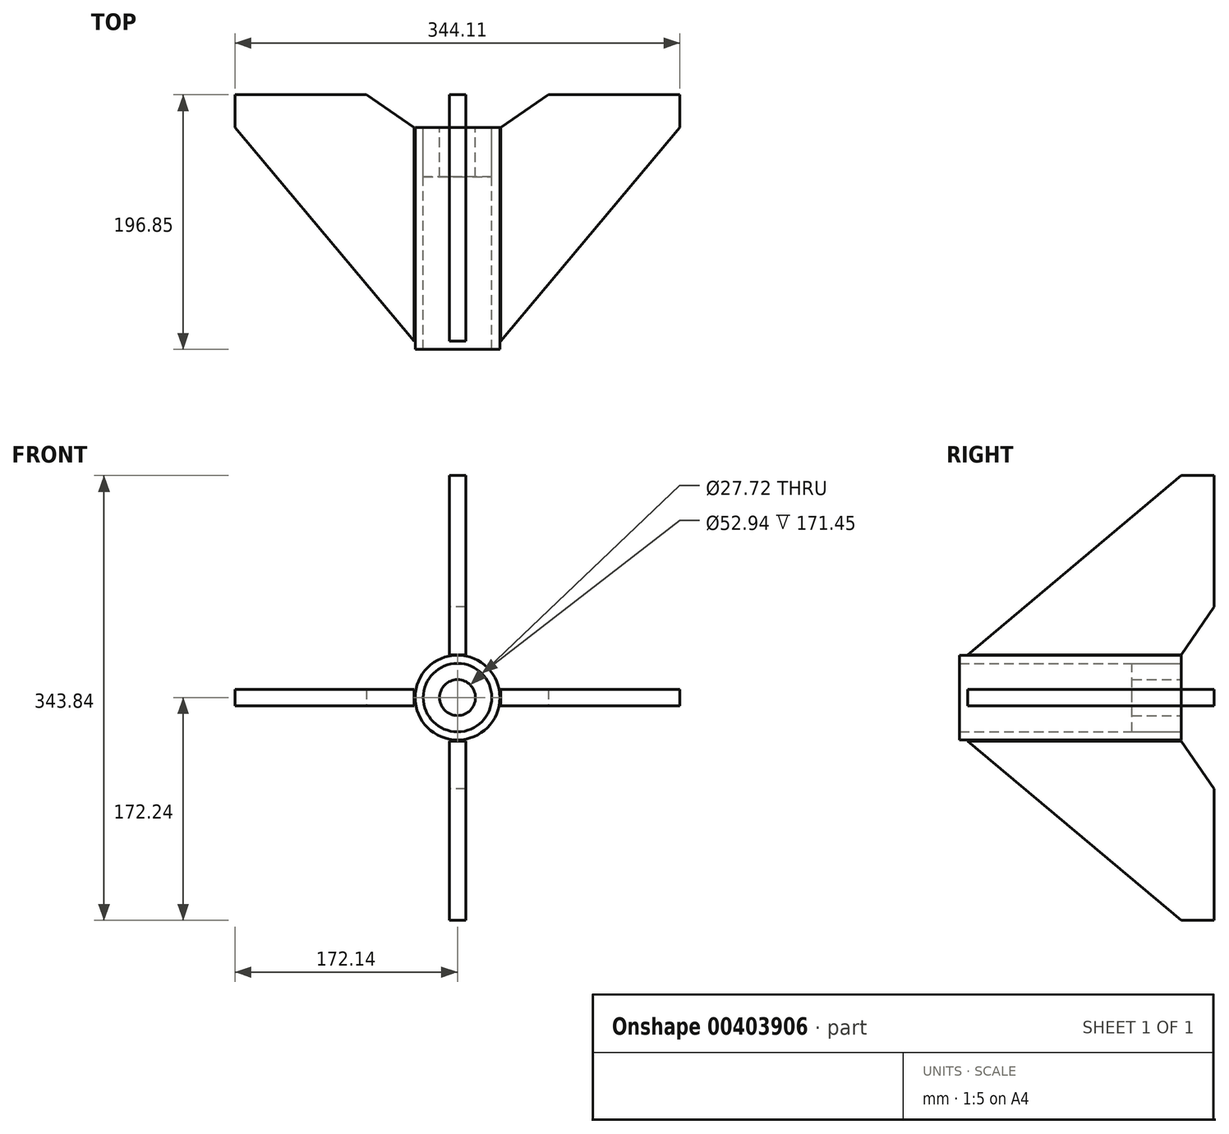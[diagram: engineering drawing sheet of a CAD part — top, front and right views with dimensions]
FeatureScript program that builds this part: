
annotation { "Feature Type Name" : "Feature", "Feature Type Description" : "" }
export const myFeature = defineFeature(function(context is Context, id is Id, definition is map)
    precondition{}
    {
        {
            var Q0;
            Q0=qCreatedBy(makeId("Front.planeOp"),FACE);
            var sketch = newSketch(context, id + "F0", { "sketchPlane" : qUnion([Q0])});
            skCircle(sketch, "E0", {"center": v(0, 0) * mm, "radius": 32.78 * mm});
            skCircle(sketch, "E1", {"center": v(0, 0) * mm, "radius": 26.47 * mm});
            skLineSegment(sketch, "E2", {"start": v(0, -76.2) * mm, "end": v(0, 76.2) * mm});
            skCircle(sketch, "E3", {"center": v(0, 0) * mm, "radius": 13.86 * mm});
            skSolve(sketch);
        }
        {
            var Q0;
            {var subQ0=sQuery(id+"F0.wireOp",EDGE,"E2");var subQ1=sQuery(id+"F0.wireOp",EDGE,"E0");var subQ2=makeQuery(id+"F0.imprint","INTERSECT",VERTEX,{"disambiguationData":[OD(1.0)],"derivedFrom":[subQ1,subQ0]});Q0=makeQuery(id+"F0.imprint","IMPRINT",FACE,{"disambiguationData":[TD([[makeQuery(id+"F0.imprint","IMPRINT",EDGE,{"disambiguationData":[TD([[subQ2,-1.0]])],"derivedFrom":subQ1}),1.0]])]});}
            var Q1;
            {var subQ0=sQuery(id+"F0.wireOp",EDGE,"E2");var subQ1=sQuery(id+"F0.wireOp",EDGE,"E0");var subQ2=makeQuery(id+"F0.imprint","INTERSECT",VERTEX,{"disambiguationData":[OD(1.0)],"derivedFrom":[subQ1,subQ0]});Q1=makeQuery(id+"F0.imprint","IMPRINT",FACE,{"disambiguationData":[TD([[makeQuery(id+"F0.imprint","IMPRINT",EDGE,{"disambiguationData":[TD([[subQ2,1.0]])],"derivedFrom":subQ1}),1.0]])]});}
            var Q2;
            {var subQ0=sQuery(id+"F0.wireOp",EDGE,"5oPWdtzy-OPul-B56H-vmQn-ATjjeZZYbcvi");var subQ1=sQuery(id+"F0.wireOp",EDGE,"E0");var subQ2=makeQuery(id+"F0.imprint","INTERSECT",VERTEX,{"disambiguationData":[OD(1.0)],"derivedFrom":[subQ1,subQ0]});Q2=makeQuery(id+"F0.imprint","IMPRINT",FACE,{"disambiguationData":[TD([[makeQuery(id+"F0.imprint","IMPRINT",EDGE,{"disambiguationData":[TD([[subQ2,-1.0]])],"derivedFrom":subQ1}),1.0]])]});}
            var Q3;
            {var subQ0=sQuery(id+"F0.wireOp",EDGE,"5oPWdtzy-OPul-B56H-vmQn-ATjjeZZYbcvi");var subQ1=sQuery(id+"F0.wireOp",EDGE,"E0");var subQ2=makeQuery(id+"F0.imprint","INTERSECT",VERTEX,{"disambiguationData":[OD(0.0)],"derivedFrom":[subQ1,subQ0]});Q3=makeQuery(id+"F0.imprint","IMPRINT",FACE,{"disambiguationData":[TD([[makeQuery(id+"F0.imprint","IMPRINT",EDGE,{"disambiguationData":[TD([[subQ2,1.0]])],"derivedFrom":subQ1}),1.0]])]});}
            var Q4;
            {var subQ0=sQuery(id+"F0.wireOp",EDGE,"E2");var subQ1=sQuery(id+"F0.wireOp",EDGE,"E0");var subQ2=makeQuery(id+"F0.imprint","INTERSECT",VERTEX,{"disambiguationData":[OD(0.0)],"derivedFrom":[subQ1,subQ0]});Q4=makeQuery(id+"F0.imprint","IMPRINT",FACE,{"disambiguationData":[TD([[makeQuery(id+"F0.imprint","IMPRINT",EDGE,{"disambiguationData":[TD([[subQ2,1.0]])],"derivedFrom":subQ1}),1.0]])]});}
            var Q5;
            {var subQ0=sQuery(id+"F0.wireOp",EDGE,"1dQYtLTc-Qprp-vLL3-yUOJ-yKbSne6VpX0o");var subQ1=sQuery(id+"F0.wireOp",EDGE,"E0");var subQ2=makeQuery(id+"F0.imprint","INTERSECT",VERTEX,{"disambiguationData":[OD(0.0)],"derivedFrom":[subQ1,subQ0]});Q5=makeQuery(id+"F0.imprint","IMPRINT",FACE,{"disambiguationData":[TD([[makeQuery(id+"F0.imprint","IMPRINT",EDGE,{"disambiguationData":[TD([[subQ2,1.0]])],"derivedFrom":subQ1}),1.0]])]});}
            var Q6;
            {var subQ0=sQuery(id+"F0.wireOp",EDGE,"E2");var subQ1=sQuery(id+"F0.wireOp",EDGE,"E0");var subQ2=makeQuery(id+"F0.imprint","INTERSECT",VERTEX,{"disambiguationData":[OD(0.0)],"derivedFrom":[subQ1,subQ0]});Q6=makeQuery(id+"F0.imprint","IMPRINT",FACE,{"disambiguationData":[TD([[makeQuery(id+"F0.imprint","IMPRINT",EDGE,{"disambiguationData":[TD([[subQ2,-1.0]])],"derivedFrom":subQ1}),1.0]])]});}
            var Q7;
            {var subQ0=sQuery(id+"F0.wireOp",EDGE,"1dQYtLTc-Qprp-vLL3-yUOJ-yKbSne6VpX0o");var subQ1=sQuery(id+"F0.wireOp",EDGE,"E0");var subQ2=makeQuery(id+"F0.imprint","INTERSECT",VERTEX,{"disambiguationData":[OD(1.0)],"derivedFrom":[subQ1,subQ0]});Q7=makeQuery(id+"F0.imprint","IMPRINT",FACE,{"disambiguationData":[TD([[makeQuery(id+"F0.imprint","IMPRINT",EDGE,{"disambiguationData":[TD([[subQ2,-1.0]])],"derivedFrom":subQ1}),1.0]])]});}
            extrude(context, id + "F1", {"entities" : qUnion([Q0, Q1, Q2, Q3, Q4, Q5, Q6, Q7]), "depth" : 171.45 * mm});
        }
        {
            var Q0;
            Q0=qCreatedBy(makeId("Right.planeOp"),FACE);
            var sketch = newSketch(context, id + "F2", { "sketchPlane" : qUnion([Q0])});
            skLineSegment(sketch, "E4", {"start": v(-165.1, -33.7) * mm, "end": v(0, -172.24) * mm});
            skLineSegment(sketch, "E5", {"start": v(-165.1, -33.7) * mm, "end": v(0, -33.7) * mm});
            skPoint(sketch, "E6", {"position": v(-165.1, 33.07) * mm});
            skLineSegment(sketch, "E7", {"start": v(-165.1, 33.07) * mm, "end": v(0, 171.6) * mm});
            skLineSegment(sketch, "E8", {"start": v(0, 33.07) * mm, "end": v(25.4, 70) * mm});
            skLineSegment(sketch, "E9", {"start": v(0, 171.6) * mm, "end": v(0, 33.07) * mm});
            skLineSegment(sketch, "E10", {"start": v(25.4, 70) * mm, "end": v(25.4, 171.6) * mm});
            skLineSegment(sketch, "E11", {"start": v(25.4, 171.6) * mm, "end": v(0, 171.6) * mm});
            skLineSegment(sketch, "E12", {"start": v(-165.1, 33.07) * mm, "end": v(0, 33.07) * mm});
            skLineSegment(sketch, "E13", {"start": v(0, -172.24) * mm, "end": v(25.4, -172.24) * mm});
            skLineSegment(sketch, "E14", {"start": v(25.4, -172.24) * mm, "end": v(25.4, -70.64) * mm});
            skLineSegment(sketch, "E15", {"start": v(25.4, -70.64) * mm, "end": v(0, -33.7) * mm});
            skSolve(sketch);
        }
        {
            var Q0;
            Q0=makeQuery(id+"F2.imprint","IMPRINT",FACE,{"disambiguationData":[TD([[makeQuery(id+"F2.imprint","IMPRINT",EDGE,{"derivedFrom":sQuery(id+"F2.wireOp",EDGE,"E4")}),1.0]])]});
            var Q1;
            Q1=makeQuery(id+"F2.imprint","IMPRINT",FACE,{"disambiguationData":[TD([[makeQuery(id+"F2.imprint","IMPRINT",EDGE,{"derivedFrom":sQuery(id+"F2.wireOp",EDGE,"8KpwZqoE-Ewsf-Pob2-hUoS-TpSoyfrnr4qn")}),1.0]])]});
            var Q2;
            Q2=makeQuery(id+"F2.imprint","IMPRINT",FACE,{"disambiguationData":[TD([[makeQuery(id+"F2.imprint","IMPRINT",EDGE,{"derivedFrom":sQuery(id+"F2.wireOp",EDGE,"E7")}),-1.0]])]});
            var Q3;
            Q3=makeQuery(id+"F2.imprint","IMPRINT",FACE,{"disambiguationData":[TD([[makeQuery(id+"F2.imprint","IMPRINT",EDGE,{"derivedFrom":sQuery(id+"F2.wireOp",EDGE,"E8")}),1.0]])]});
            extrude(context, id + "F3", {"entities" : qUnion([Q0, Q1, Q2, Q3]), "endBound" : BoundingType.SYMMETRIC, "depth" : 12.7 * mm});
        }
        {
            var Q0;
            Q0=qCreatedBy(makeId("Top.planeOp"),FACE);
            var sketch = newSketch(context, id + "F4", { "sketchPlane" : qUnion([Q0])});
            skPoint(sketch, "E16", {"position": v(33.43, -165.1) * mm});
            skPoint(sketch, "E17", {"position": v(33.43, 0) * mm});
            skLineSegment(sketch, "E18", {"start": v(33.43, -165.1) * mm, "end": v(33.43, 0) * mm});
            skLineSegment(sketch, "E19", {"start": v(33.43, -165.1) * mm, "end": v(171.97, 0) * mm});
            skLineSegment(sketch, "E20", {"start": v(33.43, 0) * mm, "end": v(70.37, 25.4) * mm});
            skLineSegment(sketch, "E21", {"start": v(171.97, 0) * mm, "end": v(171.97, 25.4) * mm});
            skLineSegment(sketch, "E22", {"start": v(171.97, 25.4) * mm, "end": v(70.37, 25.4) * mm});
            skLineSegment(sketch, "E23", {"start": v(-33.6, -165.1) * mm, "end": v(-172.14, 0) * mm});
            skLineSegment(sketch, "E24", {"start": v(-172.14, 0) * mm, "end": v(-172.14, 25.4) * mm});
            skLineSegment(sketch, "E25", {"start": v(-172.14, 25.4) * mm, "end": v(-70.54, 25.4) * mm});
            skLineSegment(sketch, "E26", {"start": v(-70.54, 25.4) * mm, "end": v(-33.6, 0) * mm});
            skLineSegment(sketch, "E27", {"start": v(-33.6, 0) * mm, "end": v(-172.14, 0) * mm});
            skLineSegment(sketch, "E28", {"start": v(-33.6, 0) * mm, "end": v(-33.6, -165.1) * mm});
            skLineSegment(sketch, "E29", {"start": v(171.97, 0) * mm, "end": v(33.43, 0) * mm});
            skSolve(sketch);
        }
        {
            var Q0;
            {var subQ0=sQuery(id+"F4.wireOp",EDGE,"E20");Q0=makeQuery(id+"F4.imprint","IMPRINT",FACE,{"disambiguationData":[TD([[makeQuery(id+"F4.imprint","IMPRINT",EDGE,{"derivedFrom":subQ0}),-1.0]])]});}
            var Q1;
            {var subQ0=sQuery(id+"F4.wireOp",EDGE,"E18");Q1=makeQuery(id+"F4.imprint","IMPRINT",FACE,{"disambiguationData":[TD([[makeQuery(id+"F4.imprint","IMPRINT",EDGE,{"derivedFrom":subQ0}),-1.0]])]});}
            var Q2;
            Q2=makeQuery(id+"F4.imprint","IMPRINT",FACE,{"disambiguationData":[TD([[makeQuery(id+"F4.imprint","IMPRINT",EDGE,{"derivedFrom":sQuery(id+"F4.wireOp",EDGE,"E24")}),-1.0]])]});
            var Q3;
            Q3=makeQuery(id+"F4.imprint","IMPRINT",FACE,{"disambiguationData":[TD([[makeQuery(id+"F4.imprint","IMPRINT",EDGE,{"derivedFrom":sQuery(id+"F4.wireOp",EDGE,"E23")}),-1.0]])]});
            extrude(context, id + "F5", {"entities" : qUnion([Q0, Q1, Q2, Q3]), "operationType" : NewBodyOperationType.ADD, "endBound" : BoundingType.SYMMETRIC, "depth" : 12.7 * mm});
        }
        {
            var Q0;
            {var subQ0=sQuery(id+"F0.wireOp",EDGE,"E2");var subQ1=sQuery(id+"F0.wireOp",EDGE,"E1");var subQ2=makeQuery(id+"F0.imprint","INTERSECT",VERTEX,{"disambiguationData":[OD(0.0)],"derivedFrom":[subQ1,subQ0]});Q0=makeQuery(id+"F0.imprint","IMPRINT",FACE,{"disambiguationData":[TD([[makeQuery(id+"F0.imprint","IMPRINT",EDGE,{"disambiguationData":[TD([[subQ2,-1.0]])],"derivedFrom":subQ1}),1.0]])]});}
            var sketch = newSketch(context, id + "F6", { "sketchPlane" : qUnion([Q0])});
            skCircle(sketch, "E30", {"center": v(0, 0) * mm, "radius": 12.7 * mm});
            skSolve(sketch);
        }
        {
            var Q0;
            {var subQ0=sQuery(id+"F0.wireOp",EDGE,"E2");var subQ1=sQuery(id+"F0.wireOp",EDGE,"E1");var subQ2=makeQuery(id+"F0.imprint","INTERSECT",VERTEX,{"disambiguationData":[OD(0.0)],"derivedFrom":[subQ1,subQ0]});Q0=makeQuery(id+"F0.imprint","IMPRINT",FACE,{"disambiguationData":[TD([[makeQuery(id+"F0.imprint","IMPRINT",EDGE,{"disambiguationData":[TD([[subQ2,1.0]])],"derivedFrom":subQ1}),1.0]])]});}
            var Q1;
            {var subQ0=sQuery(id+"F0.wireOp",EDGE,"E2");var subQ1=sQuery(id+"F0.wireOp",EDGE,"E1");var subQ2=makeQuery(id+"F0.imprint","INTERSECT",VERTEX,{"disambiguationData":[OD(0.0)],"derivedFrom":[subQ1,subQ0]});Q1=makeQuery(id+"F0.imprint","IMPRINT",FACE,{"disambiguationData":[TD([[makeQuery(id+"F0.imprint","IMPRINT",EDGE,{"disambiguationData":[TD([[subQ2,-1.0]])],"derivedFrom":subQ1}),1.0]])]});}
            var Q2;
            Q2=sQuery(id+"F6.wireOp",EDGE,"E30");
            var Q3;
            Q3=sQuery(id+"F0.wireOp",EDGE,"E1");
            extrude(context, id + "F7", {"entities" : qUnion([Q0, Q1]), "surfaceEntities" : qUnion([Q2, Q3]), "depth" : 38.1 * mm});
        }
    });
